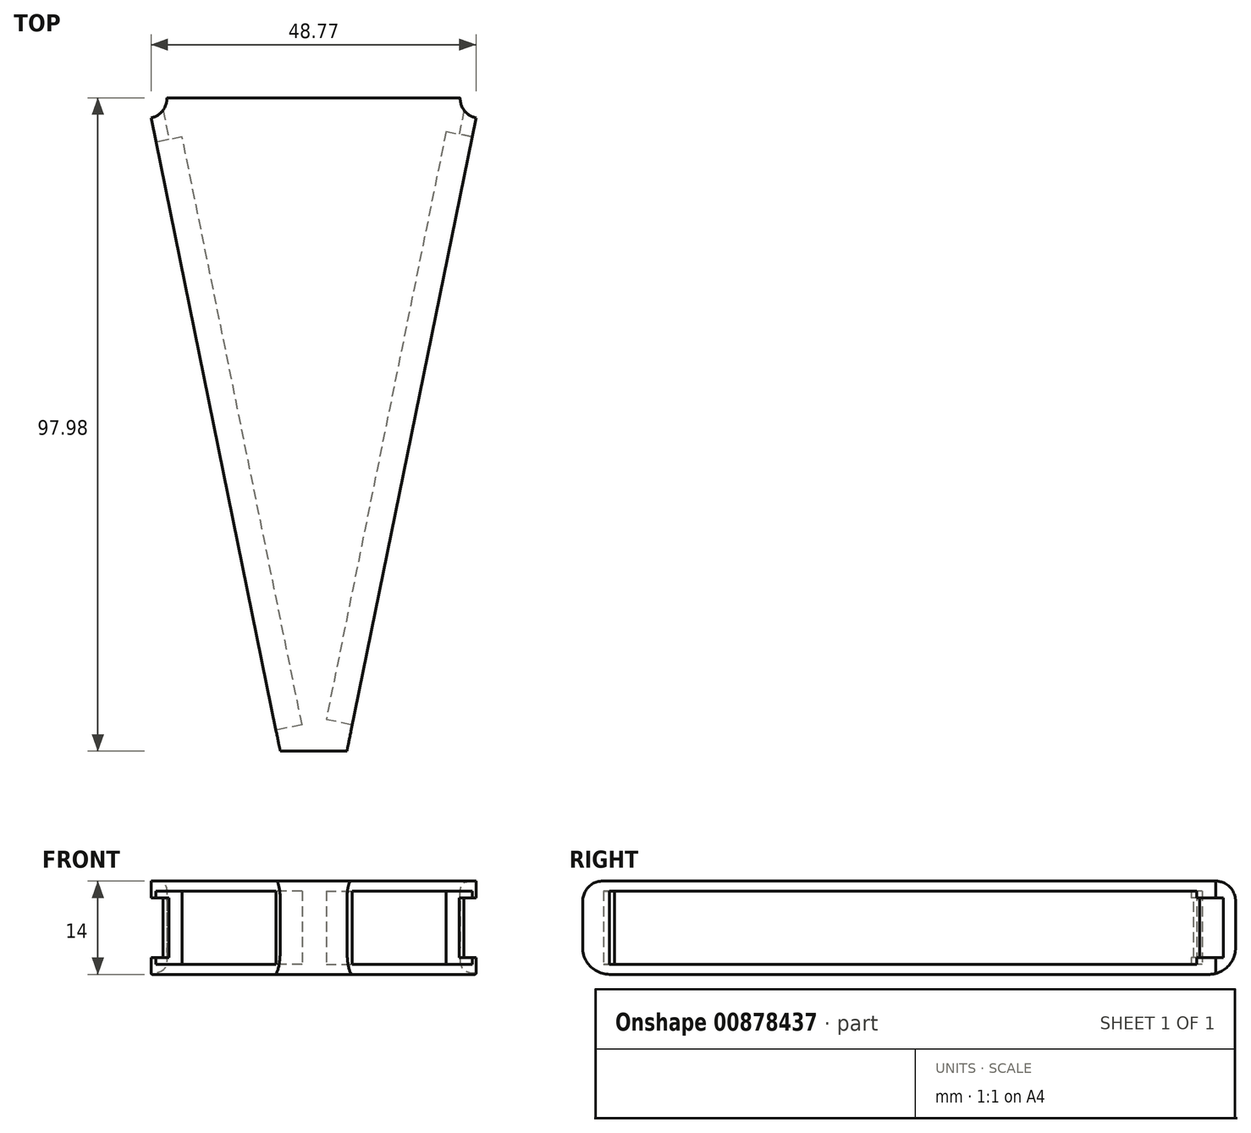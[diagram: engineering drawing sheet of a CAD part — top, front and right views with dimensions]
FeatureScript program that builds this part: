
annotation { "Feature Type Name" : "Feature", "Feature Type Description" : "" }
export const myFeature = defineFeature(function(context is Context, id is Id, definition is map)
    precondition{}
    {
        {
            var Q0;
            Q0=qCreatedBy(makeId("Top.planeOp"),FACE);
            var sketch = newSketch(context, id + "F0", { "sketchPlane" : qUnion([Q0])});
            skPoint(sketch, "E0.middle", {"position": v(131.32, 0) * mm});
            skLineSegment(sketch, "E1", {"start": v(-25, 50.12) * mm, "end": v(25, 50.12) * mm});
            skLineSegment(sketch, "E2", {"start": v(-25, 50.12) * mm, "end": v(-5, -47.86) * mm});
            skLineSegment(sketch, "E3", {"start": v(-5, -47.86) * mm, "end": v(5, -47.86) * mm});
            skLineSegment(sketch, "E4", {"start": v(5, -47.86) * mm, "end": v(25, 50.12) * mm});
            skLineSegment(sketch, "E5.bottom", {"start": v(151.82, -50) * mm, "end": v(110.82, -50) * mm});
            skLineSegment(sketch, "E5.top", {"start": v(151.82, 50) * mm, "end": v(110.82, 50) * mm});
            skLineSegment(sketch, "E5.left", {"start": v(151.82, -50) * mm, "end": v(151.82, 50) * mm});
            skLineSegment(sketch, "E5.right", {"start": v(110.82, -50) * mm, "end": v(110.82, 50) * mm});
            skPoint(sketch, "E5.middle", {"position": v(0, 5.03) * mm});
            skLineSegment(sketch, "E6.bottom", {"start": v(-25, 50.12) * mm, "end": v(-22, 50.12) * mm});
            skLineSegment(sketch, "E6.top", {"start": v(-25, 47.12) * mm, "end": v(-22, 47.12) * mm});
            skLineSegment(sketch, "E6.left", {"start": v(-25, 50.12) * mm, "end": v(-25, 47.12) * mm});
            skLineSegment(sketch, "E6.right", {"start": v(-22, 50.12) * mm, "end": v(-22, 47.12) * mm});
            skLineSegment(sketch, "E7.bottom", {"start": v(25, 50.12) * mm, "end": v(22, 50.12) * mm});
            skLineSegment(sketch, "E7.top", {"start": v(25, 47.12) * mm, "end": v(22, 47.12) * mm});
            skLineSegment(sketch, "E7.left", {"start": v(25, 50.12) * mm, "end": v(25, 47.12) * mm});
            skLineSegment(sketch, "E7.right", {"start": v(22, 50.12) * mm, "end": v(22, 47.12) * mm});
            skSolve(sketch);
        }
        {
            var Q0;
            {var subQ1=sQuery(id+"F0.wireOp",EDGE,"E3");Q0=makeQuery(id+"F0.imprint","IMPRINT",FACE,{"disambiguationData":[TD([[makeQuery(id+"F0.imprint","IMPRINT",EDGE,{"derivedFrom":subQ1}),1.0]])]});}
            var Q1;
            Q1 = qSketchRegion(id + "Fp16FwaSlMcaFCo_1", true);
            extrude(context, id + "F1", {"entities" : qUnion([Q0, Q1]), "endBound" : BoundingType.SYMMETRIC, "depth" : 14 * mm, "offsetDistance" : 25.4 * mm});
        }
        {
            var Q0;
            Q0=makeQuery(id+"F1.opExtrude","SWEPT_FACE",FACE,{"disambiguationData":[OSD([sQuery(id+"F0.wireOp",EDGE,"E2")])]});
            var sketch = newSketch(context, id + "F2", { "sketchPlane" : qUnion([Q0])});
            skLineSegment(sketch, "E8.bottom", {"start": v(42.68, 5.5) * mm, "end": v(-47.32, 5.5) * mm});
            skLineSegment(sketch, "E8.top", {"start": v(42.68, -5.5) * mm, "end": v(-47.32, -5.5) * mm});
            skLineSegment(sketch, "E8.left", {"start": v(42.68, 5.5) * mm, "end": v(42.68, -5.5) * mm});
            skLineSegment(sketch, "E8.right", {"start": v(-47.32, 5.5) * mm, "end": v(-47.32, -5.5) * mm});
            skPoint(sketch, "E8.middle", {"position": v(-2.32, 0) * mm});
            skLineSegment(sketch, "E9.bottom", {"start": v(-57.27, 4.5) * mm, "end": v(-44.77, 4.5) * mm});
            skLineSegment(sketch, "E9.top", {"start": v(-57.27, -4.5) * mm, "end": v(-44.77, -4.5) * mm});
            skLineSegment(sketch, "E9.left", {"start": v(-57.27, 4.5) * mm, "end": v(-57.27, -4.5) * mm});
            skLineSegment(sketch, "E9.right", {"start": v(-44.77, 4.5) * mm, "end": v(-44.77, -4.5) * mm});
            skSolve(sketch);
        }
        {
            var Q0;
            Q0=makeQuery(id+"F2.imprint","IMPRINT",FACE,{"disambiguationData":[TD([[makeQuery(id+"F2.imprint","IMPRINT",EDGE,{"derivedFrom":sQuery(id+"F2.wireOp",EDGE,"E8.bottom")}),1.0]])]});
            var Q1;
            {var subQ5=sQuery(id+"F2.wireOp",EDGE,"E9.right");Q1=makeQuery(id+"F2.imprint","IMPRINT",FACE,{"disambiguationData":[TD([[makeQuery(id+"F2.imprint","IMPRINT",EDGE,{"derivedFrom":subQ5}),-1.0]])]});}
            extrude(context, id + "F3", {"entities" : qUnion([Q0, Q1]), "operationType" : NewBodyOperationType.REMOVE, "oppositeDirection" : true, "depth" : 4 * mm, "offsetDistance" : 25.4 * mm});
        }
        {
            var Q0;
            {var subQ0=sQuery(id+"F2.wireOp",EDGE,"E9.bottom");var subQ1=sQuery(id+"F2.wireOp",EDGE,"E8.right");var subQ2=makeQuery(id+"F2.imprint","INTERSECT",VERTEX,{"derivedFrom":[subQ1,subQ0]});Q0=makeQuery(id+"F2.imprint","IMPRINT",FACE,{"disambiguationData":[TD([[makeQuery(id+"F2.imprint","IMPRINT",EDGE,{"disambiguationData":[TD([[subQ2,-1.0]])],"derivedFrom":subQ1}),-1.0]])]});}
            var Q1;
            {var subQ0=sQuery(id+"F2.wireOp",EDGE,"E9.left");Q1=makeQuery(id+"F2.imprint","IMPRINT",FACE,{"disambiguationData":[TD([[makeQuery(id+"F2.imprint","IMPRINT",EDGE,{"derivedFrom":subQ0}),1.0]])]});}
            var Q2;
            {var subQ5=sQuery(id+"F2.wireOp",EDGE,"E9.right");Q2=makeQuery(id+"F2.imprint","IMPRINT",FACE,{"disambiguationData":[TD([[makeQuery(id+"F2.imprint","IMPRINT",EDGE,{"derivedFrom":subQ5}),-1.0]])]});}
            extrude(context, id + "F4", {"entities" : qUnion([Q0, Q1, Q2]), "operationType" : NewBodyOperationType.REMOVE, "oppositeDirection" : true, "depth" : 2 * mm, "offsetDistance" : 25.4 * mm});
        }
        {
            var Q0;
            Q0=makeQuery(id+"F1.opExtrude","SWEPT_FACE",FACE,{"disambiguationData":[OSD([sQuery(id+"F0.wireOp",EDGE,"E4")])]});
            var sketch = newSketch(context, id + "F5", { "sketchPlane" : qUnion([Q0])});
            skLineSegment(sketch, "E10.bottom", {"start": v(48.18, 5.5) * mm, "end": v(-41.82, 5.5) * mm});
            skLineSegment(sketch, "E10.top", {"start": v(48.18, -5.5) * mm, "end": v(-41.82, -5.5) * mm});
            skLineSegment(sketch, "E10.left", {"start": v(48.18, 5.5) * mm, "end": v(48.18, -5.5) * mm});
            skLineSegment(sketch, "E10.right", {"start": v(-41.82, 5.5) * mm, "end": v(-41.82, -5.5) * mm});
            skPoint(sketch, "E10.middle", {"position": v(3.18, 0) * mm});
            skLineSegment(sketch, "E11.bottom", {"start": v(57.5, 4.5) * mm, "end": v(46.05, 4.5) * mm});
            skLineSegment(sketch, "E11.top", {"start": v(57.5, -4.5) * mm, "end": v(46.05, -4.5) * mm});
            skLineSegment(sketch, "E11.left", {"start": v(57.5, 4.5) * mm, "end": v(57.5, -4.5) * mm});
            skLineSegment(sketch, "E11.right", {"start": v(46.05, 4.5) * mm, "end": v(46.05, -4.5) * mm});
            skSolve(sketch);
        }
        {
            var Q0;
            {var subQ4=sQuery(id+"F5.wireOp",EDGE,"E10.bottom");Q0=makeQuery(id+"F5.imprint","IMPRINT",FACE,{"disambiguationData":[TD([[makeQuery(id+"F5.imprint","IMPRINT",EDGE,{"derivedFrom":subQ4}),1.0]])]});}
            var Q1;
            {var subQ5=sQuery(id+"F5.wireOp",EDGE,"E11.right");Q1=makeQuery(id+"F5.imprint","IMPRINT",FACE,{"disambiguationData":[TD([[makeQuery(id+"F5.imprint","IMPRINT",EDGE,{"derivedFrom":subQ5}),1.0]])]});}
            extrude(context, id + "F6", {"entities" : qUnion([Q0, Q1]), "operationType" : NewBodyOperationType.REMOVE, "oppositeDirection" : true, "depth" : 4 * mm, "offsetDistance" : 25.4 * mm});
        }
        {
            var Q0;
            {var subQ0=sQuery(id+"F5.wireOp",EDGE,"E11.bottom");var subQ1=sQuery(id+"F5.wireOp",EDGE,"E10.left");var subQ2=makeQuery(id+"F5.imprint","INTERSECT",VERTEX,{"derivedFrom":[subQ1,subQ0]});Q0=makeQuery(id+"F5.imprint","IMPRINT",FACE,{"disambiguationData":[TD([[makeQuery(id+"F5.imprint","IMPRINT",EDGE,{"disambiguationData":[TD([[subQ2,-1.0]])],"derivedFrom":subQ1}),1.0]])]});}
            var Q1;
            {var subQ0=sQuery(id+"F5.wireOp",EDGE,"E11.left");Q1=makeQuery(id+"F5.imprint","IMPRINT",FACE,{"disambiguationData":[TD([[makeQuery(id+"F5.imprint","IMPRINT",EDGE,{"derivedFrom":subQ0}),-1.0]])]});}
            var Q2;
            {var subQ5=sQuery(id+"F5.wireOp",EDGE,"E11.right");Q2=makeQuery(id+"F5.imprint","IMPRINT",FACE,{"disambiguationData":[TD([[makeQuery(id+"F5.imprint","IMPRINT",EDGE,{"derivedFrom":subQ5}),1.0]])]});}
            extrude(context, id + "F7", {"entities" : qUnion([Q0, Q1, Q2]), "operationType" : NewBodyOperationType.REMOVE, "oppositeDirection" : true, "depth" : 2 * mm, "offsetDistance" : 25.4 * mm});
        }
        {
            var Q0;
            Q0=makeQuery(id+"F1.opExtrude","SWEPT_EDGE",EDGE,{"disambiguationData":[OSD([sQuery(id+"F0.wireOp",EDGE,"E7.top"),sQuery(id+"F0.wireOp",EDGE,"E7.right")])]});
            var Q1;
            Q1=makeQuery(id+"F1.opExtrude","SWEPT_EDGE",EDGE,{"disambiguationData":[OSD([sQuery(id+"F0.wireOp",EDGE,"E6.top"),sQuery(id+"F0.wireOp",EDGE,"E6.right")])]});
            fillet(context, id + "F8", {"entities" : qUnion([Q0, Q1]), "radius" : 3 * mm, "tangentPropagation" : true, "allowEdgeOverflow" : false});
        }
        {
            var Q0;
            Q0=makeQuery(id+"F1.opExtrude","CAP_EDGE",EDGE,{"disambiguationData":[OSD([sQuery(id+"F0.wireOp",EDGE,"E1")])],"isStart":false});
            var Q1;
            Q1=makeQuery(id+"F1.opExtrude","CAP_EDGE",EDGE,{"disambiguationData":[OSD([sQuery(id+"F0.wireOp",EDGE,"E3")])],"isStart":false});
            fillet(context, id + "F9", {"entities" : qUnion([Q0, Q1]), "radius" : 3 * mm, "tangentPropagation" : true, "allowEdgeOverflow" : false});
        }
        {
            var Q0;
            Q0=makeQuery(id+"F1.opExtrude","CAP_EDGE",EDGE,{"disambiguationData":[OSD([sQuery(id+"F0.wireOp",EDGE,"E1")])],"isStart":true});
            var Q1;
            Q1=makeQuery(id+"F1.opExtrude","CAP_EDGE",EDGE,{"disambiguationData":[OSD([sQuery(id+"F0.wireOp",EDGE,"E3")])],"isStart":true});
            fillet(context, id + "F10", {"entities" : qUnion([Q0, Q1]), "radius" : 4 * mm, "tangentPropagation" : true, "allowEdgeOverflow" : false});
        }
    });
